# Revit family: YVPT-S240-14K(設計震度1G以下)
name_source: partatom
category: スプリンクラ
revit_build: Autodesk Revit 2018 (Build: 20170223_1515(x64)
units: mm (PartAtom-declared; Revit-internal decimal feet)

## family parameters
OmniClass タイトル = Foam Fire Fighting Terminals
OmniClass 番号 = 23.65.70.17.21
パーツ タイプ = 標準
ロード時にボイドで切り取り = いいえ
丸型コネクタ寸法 = 直径を使用
作業面ベース = いいえ
共有 = いいえ
常に垂直 = はい
注釈の向きを維持 = いいえ
部屋計算ポイント = いいえ

## types (1)
- YVPT-S240-14K(設計震度1G以下)
    Clearance Back = 0  [stored 0 ft]
    Clearance Front = 0  [stored 0 ft]
    Clearance Left = 0  [stored 0 ft]
    Clearance Right = 0  [stored 0 ft]
    Clearance Top = 0  [stored 0 ft]
    Depth = 0  [stored 0 ft]
    Height = 0  [stored 0 ft]
    IfcExportAs = IfcFireSuppressionTerminalType
    IfcExportType = SPRINKLER
    OmniClassCode = 23-29 33 13 21
    ProductInformation = https://www.yamatoprotec.co.jp
    URL = https://www.yamatoprotec.co.jp
    Uniclass2015Code = Pr_60_50_67_31
    Uniclass2015Title = Foam fire fighting tanks
    Uniclass2015Version = Systems v1.9
    Width = 0  [stored 0 ft]
    アセンブリ コード = D4090200
    キーノート = 13955
    モデル = YVPT-S240-14K
    仕様書バージョン = Version1.0
    企業コード = 580077214
    分類コード = 50903001800000
    呼称 = YVPT-S240-14K
    容量 = 268.0 L
    最高使用圧力 = 0.0 Pa
    機械基礎_D = 0  [stored 0 ft]
    機械基礎_H = 0  [stored 0 ft]
    機械基礎_W = 0  [stored 0 ft]
    積算_科目 = 9 消火設備
    製品質量 = 255.00 kg
    製造元 = ヤマトプロテック株式会社
    説明 = YVPT-S240-14K
    質量 = 0.00 kg
    運転質量 = 0.00 kg

note: [stored X ft] marks values corroborated as IEEE doubles in the binary element streams (Revit-internal decimal feet)
